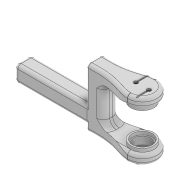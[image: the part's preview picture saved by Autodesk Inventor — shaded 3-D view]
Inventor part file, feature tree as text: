
AUTODESK INVENTOR PART (.ipt)
format: ipt  version: 2020 (Build 240168000, 168)  size: 550,400 bytes
history: native  units: mm
features: extrude x8, sketch x8, fillet x6, mirror x2, plane x1, projected_geometry x1
ambient origin geometry x8: Origin, YZ Plane, XZ Plane, XY Plane, X Axis, Y Axis, Z Axis, Center Point
bodies: Solid1 (feature_tree)
feature tree (26):
  extrude  "Extrusion1"  Depth=18.0mm
  extrude  "Extrusion2"  Depth=4.5mm
  extrude  "Extrusion3"  Depth=9.0mm
  extrude  "Extrusion4"  Depth=22.0mm
  extrude  "Extrusion5"  Depth=22.0mm
  extrude  "Extrusion6"  Depth=5.0mm
  plane  "Work Plane1"
  mirror  "Mirror1"
  extrude  "Extrusion7"  Depth=14.0mm
  fillet  "Fillet8"  Radius=3.0mm
  fillet  "Fillet9"  Radius=14.0mm
  fillet  "Fillet10"  Radius=16.0mm
  fillet  "Fillet11"  Radius=5.2mm
  extrude  "Extrusion9"  Depth=5.2mm
  mirror  "Mirror3"
  fillet  "Fillet12"  Radius=2.4mm
  fillet  "Fillet13"  Radius=7.0mm
  sketch  "Sketch1"  dims[d0=41.0mm d1=18.0mm]
  sketch  "Sketch3"  dims[d2=9.0mm d3=0.0mm d4=4.5mm]
  sketch  "Sketch4"  dims[d5=5.0mm d6=9.0mm]
  sketch  "Sketch5"  dims[d7=2.5mm d8=22.0mm]
  sketch  "Sketch6"  dims[d9=0.0mm d10=0.0mm d11=22.0mm]
  sketch  "Sketch7"  dims[d12=2.0mm d13=5.0mm]
  sketch  "Sketch8"  dims[d14=3.0mm d15=14.0mm d16=3.0mm d17=14.0mm d18=16.0mm d19=0.0mm d23=5.2mm]
  projected_geometry  "Projected Loop1"
  sketch  "Sketch11"  dims[d24=2.4mm d25=0.0mm d26=5.2mm d27=2.4mm d28=0.0mm d29=7.0mm d30=6.0mm d31=1.0mm d32=0.0mm d37=2.0mm d38=17.5mm d39=0.75mm d40=0.0mm d41=0.0mm d46=5.2mm d47=2.0mm d48=2.0mm d49=1.0mm d50=1.0mm d51=1.0mm d52=0.2mm d54=0.24mm d55=0.0mm d56=0.5mm d57=0.5mm]
